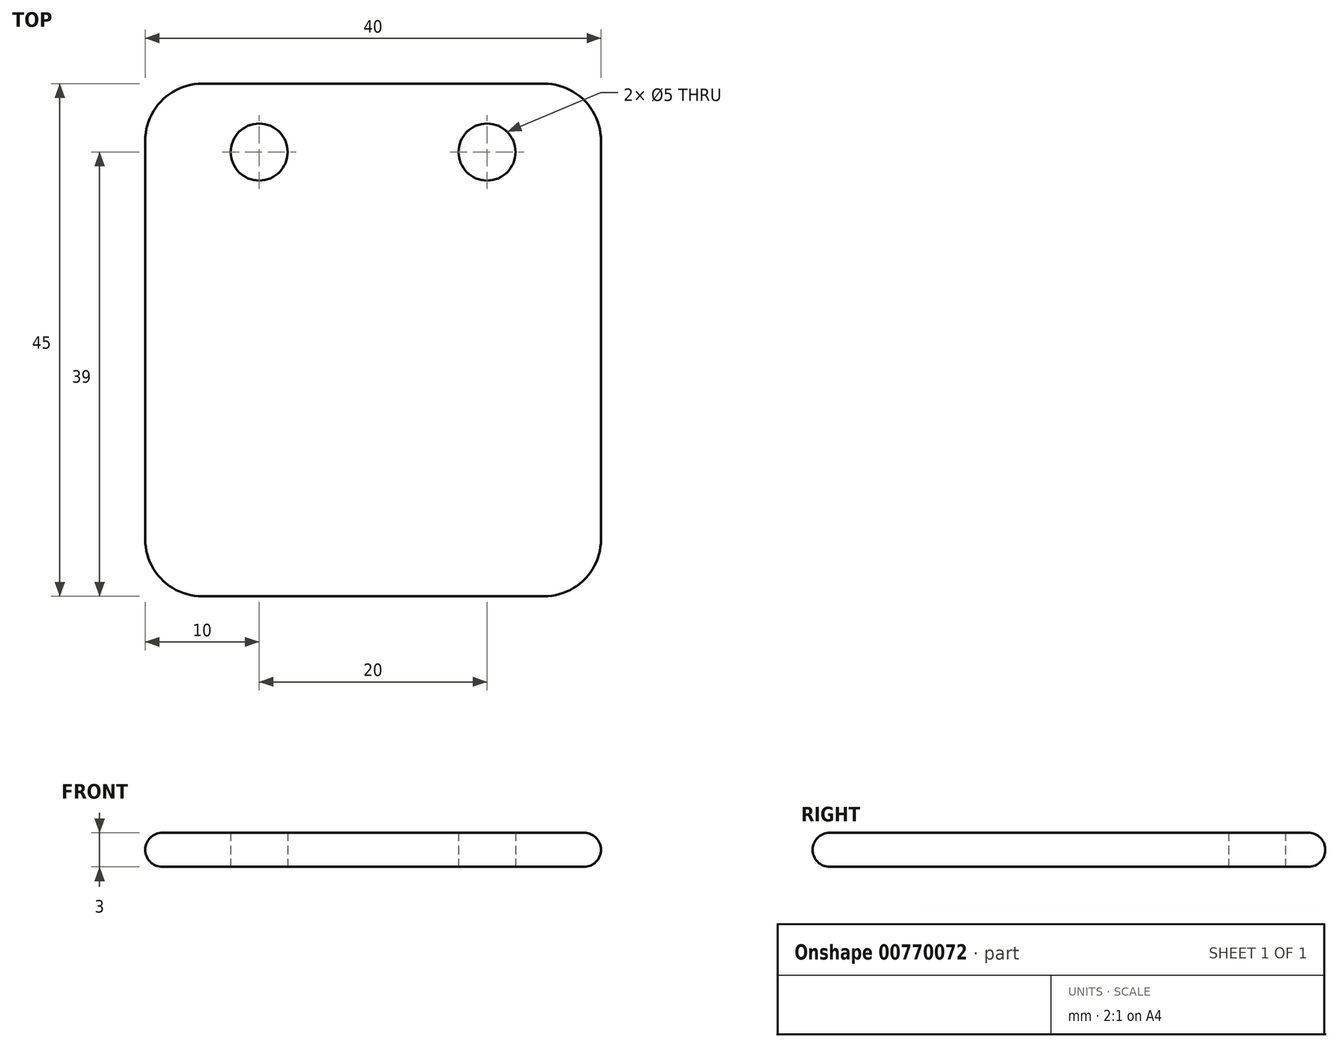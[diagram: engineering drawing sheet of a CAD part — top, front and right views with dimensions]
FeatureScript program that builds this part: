
annotation { "Feature Type Name" : "Feature", "Feature Type Description" : "" }
export const myFeature = defineFeature(function(context is Context, id is Id, definition is map)
    precondition{}
    {
        {
            var Q0;
            Q0=qCreatedBy(makeId("Top.planeOp"),FACE);
            var sketch = newSketch(context, id + "F0", { "sketchPlane" : qUnion([Q0])});
            skLineSegment(sketch, "E0.bottom", {"start": v(15, 22.5) * mm, "end": v(-15, 22.5) * mm});
            skLineSegment(sketch, "E0.top", {"start": v(15, -22.5) * mm, "end": v(-15, -22.5) * mm});
            skLineSegment(sketch, "E0.left", {"start": v(20, 17.5) * mm, "end": v(20, -17.5) * mm});
            skLineSegment(sketch, "E0.right", {"start": v(-20, 17.5) * mm, "end": v(-20, -17.5) * mm});
            skPoint(sketch, "E0.middle", {"position": v(0, 0) * mm});
            skCircle(sketch, "E1", {"center": v(-10, 16.5) * mm, "radius": 2.5 * mm});
            skCircle(sketch, "E2", {"center": v(10, 16.5) * mm, "radius": 2.5 * mm});
            skPoint(sketch, "E3.visualSharp", {"position": v(-20, 22.5) * mm});
            skArc(sketch, "E3.filletArc", {"start": v(-15, 22.5) * mm, "mid": v(-18.54, 21.04) * mm, "end": v(-20, 17.5) * mm});
            skPoint(sketch, "E4.visualSharp", {"position": v(20, 22.5) * mm});
            skArc(sketch, "E4.filletArc", {"start": v(20, 17.5) * mm, "mid": v(18.54, 21.04) * mm, "end": v(15, 22.5) * mm});
            skPoint(sketch, "E5.visualSharp", {"position": v(20, -22.5) * mm});
            skArc(sketch, "E5.filletArc", {"start": v(15, -22.5) * mm, "mid": v(18.54, -21.04) * mm, "end": v(20, -17.5) * mm});
            skPoint(sketch, "E6.visualSharp", {"position": v(-20, -22.5) * mm});
            skArc(sketch, "E6.filletArc", {"start": v(-20, -17.5) * mm, "mid": v(-18.54, -21.04) * mm, "end": v(-15, -22.5) * mm});
            skSolve(sketch);
        }
        {
            var Q0;
            Q0 = qSketchRegion(id + "F0", true);
            extrude(context, id + "F1", {"entities" : qUnion([Q0]), "depth" : 3 * mm, "offsetDistance" : 25 * mm});
        }
        {
            var Q0;
            Q0=makeQuery(id+"F1.opExtrude","CAP_EDGE",EDGE,{"disambiguationData":[OSD([sQuery(id+"F0.wireOp",EDGE,"E0.right")])],"isStart":false});
            var Q1;
            Q1=makeQuery(id+"F1.opExtrude","CAP_EDGE",EDGE,{"disambiguationData":[OSD([sQuery(id+"F0.wireOp",EDGE,"E0.right")])],"isStart":true});
            fillet(context, id + "F2", {"entities" : qUnion([Q0, Q1]), "radius" : 1.5 * mm, "tangentPropagation" : true, "allowEdgeOverflow" : false});
        }
    });
